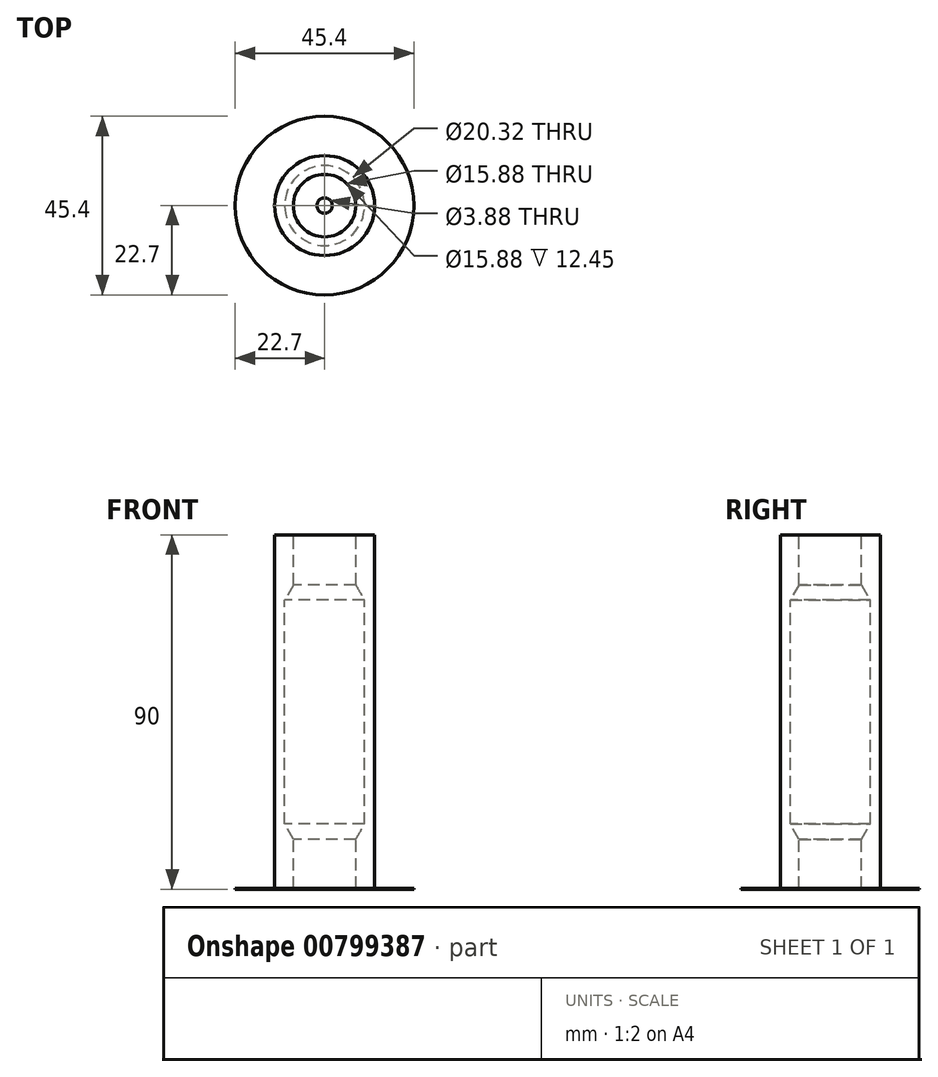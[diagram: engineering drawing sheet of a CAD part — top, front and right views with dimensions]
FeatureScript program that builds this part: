
annotation { "Feature Type Name" : "Feature", "Feature Type Description" : "" }
export const myFeature = defineFeature(function(context is Context, id is Id, definition is map)
    precondition{}
    {
        {
            var Q0;
            Q0=qCreatedBy(makeId("Front.planeOp"),FACE);
            var sketch = newSketch(context, id + "F0", { "sketchPlane" : qUnion([Q0])});
            skLineSegment(sketch, "E0", {"start": v(-12.7, -44.75) * mm, "end": v(-12.7, 45) * mm});
            skLineSegment(sketch, "E1", {"start": v(-12.7, 45) * mm, "end": v(-7.94, 45) * mm});
            skLineSegment(sketch, "E2", {"start": v(-7.94, 45) * mm, "end": v(-7.94, 32.3) * mm});
            skLineSegment(sketch, "E3", {"start": v(-10.16, 28.45) * mm, "end": v(-7.94, 32.3) * mm});
            skLineSegment(sketch, "E4", {"start": v(-10.16, 28.45) * mm, "end": v(-10.16, -28.45) * mm});
            skLineSegment(sketch, "E5", {"start": v(-10.16, -28.45) * mm, "end": v(-7.94, -32.3) * mm});
            skLineSegment(sketch, "E6", {"start": v(-7.94, -32.3) * mm, "end": v(-7.94, -44.75) * mm});
            skLineSegment(sketch, "E7", {"start": v(-7.94, -45) * mm, "end": v(-12.7, -45) * mm});
            skLineSegment(sketch, "E8", {"start": v(-7.94, -45) * mm, "end": v(-1.94, -45) * mm});
            skLineSegment(sketch, "E9", {"start": v(-1.94, -45) * mm, "end": v(-1.94, -44.75) * mm});
            skLineSegment(sketch, "E10", {"start": v(-1.94, -44.75) * mm, "end": v(-7.94, -44.75) * mm});
            skLineSegment(sketch, "E11", {"start": v(-12.7, -45) * mm, "end": v(-22.7, -45) * mm});
            skLineSegment(sketch, "E12", {"start": v(-22.7, -45) * mm, "end": v(-22.7, -44.75) * mm});
            skLineSegment(sketch, "E13", {"start": v(-22.7, -44.75) * mm, "end": v(-12.7, -44.75) * mm});
            skLineSegment(sketch, "E14", {"start": v(0, 68.18) * mm, "end": v(0, -60.07) * mm});
            skSolve(sketch);
        }
        {
            var Q0;
            Q0=makeQuery(id+"F0.imprint","IMPRINT",FACE,{"disambiguationData":[TD([[makeQuery(id+"F0.imprint","IMPRINT",EDGE,{"derivedFrom":sQuery(id+"F0.wireOp",EDGE,"E0")}),-1.0]])]});
            var Q1;
            Q1=sQuery(id+"F0.wireOp",EDGE,"E14");
            revolve(context, id + "F1", {"surfaceOperationType" : NewSurfaceOperationType.NEW, "entities" : qUnion([Q0]), "axis" : qUnion([Q1]), "revolveType" : RevolveType.FULL});
        }
    });
